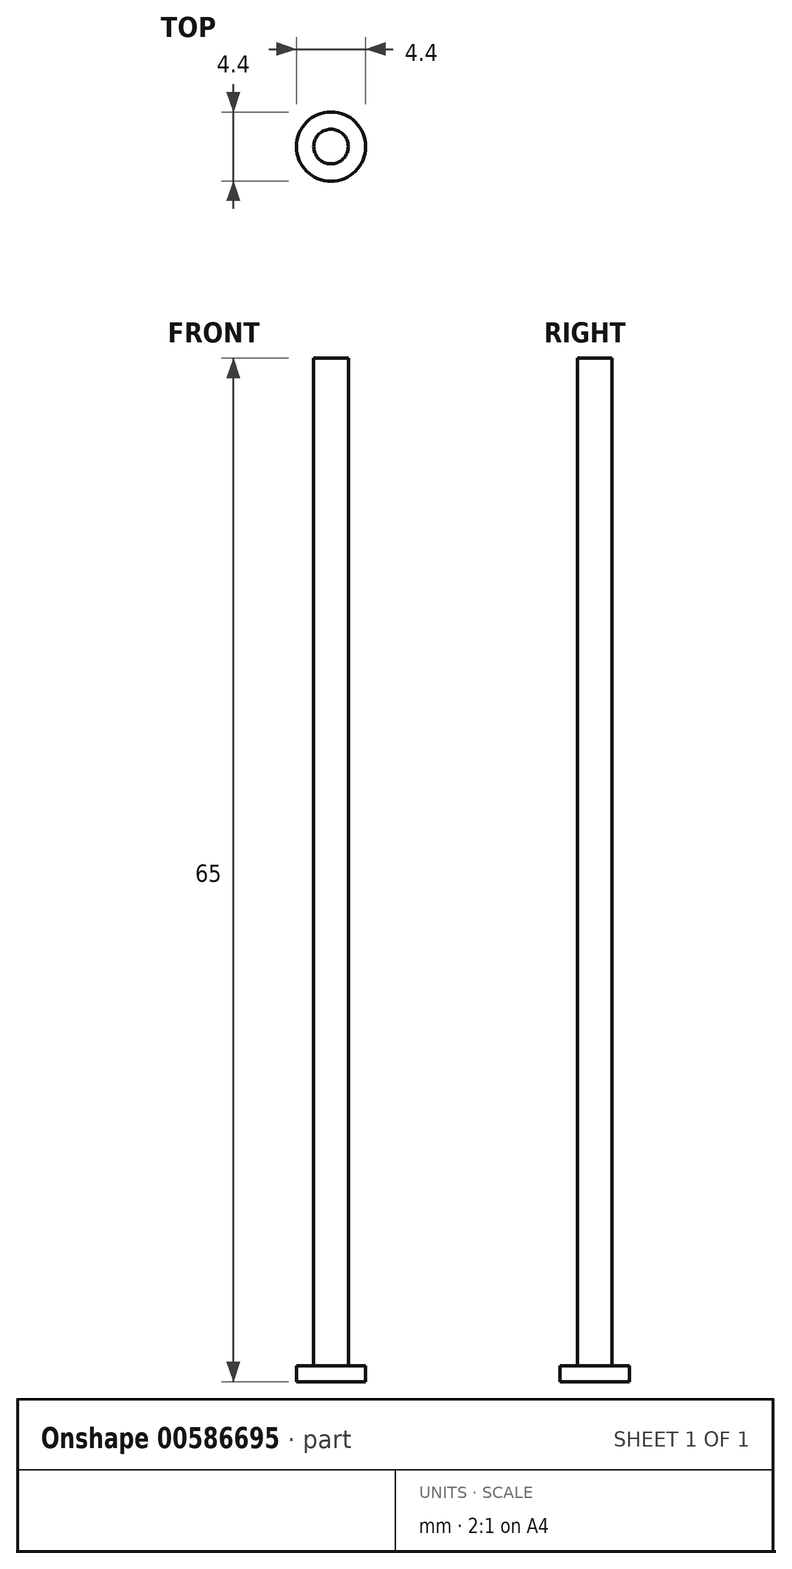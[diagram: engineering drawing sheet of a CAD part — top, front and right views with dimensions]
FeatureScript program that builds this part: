
annotation { "Feature Type Name" : "Feature", "Feature Type Description" : "" }
export const myFeature = defineFeature(function(context is Context, id is Id, definition is map)
    precondition{}
    {
        {
            var Q0;
            Q0=qCreatedBy(makeId("Top.planeOp"),FACE);
            var sketch = newSketch(context, id + "F0", { "sketchPlane" : qUnion([Q0])});
            skCircle(sketch, "E0", {"center": v(0, 0) * mm, "radius": 1.1 * mm});
            skSolve(sketch);
        }
        {
            var Q0;
            Q0 = qSketchRegion(id + "F0", true);
            extrude(context, id + "F1", {"entities" : qUnion([Q0]), "depth" : 64 * mm, "offsetDistance" : 25 * mm});
        }
        {
            var Q0;
            Q0=qCreatedBy(makeId("Top.planeOp"),FACE);
            var sketch = newSketch(context, id + "F2", { "sketchPlane" : qUnion([Q0])});
            skCircle(sketch, "E1", {"center": v(0, 0) * mm, "radius": 2.2 * mm});
            skSolve(sketch);
        }
        {
            var Q0;
            Q0=makeQuery(id+"F2.imprint","IMPRINT",FACE,{"disambiguationData":[TD([[makeQuery(id+"F2.imprint","IMPRINT",EDGE,{"derivedFrom":sQuery(id+"F2.wireOp",EDGE,"E1")}),1.0]])]});
            extrude(context, id + "F3", {"entities" : qUnion([Q0]), "operationType" : NewBodyOperationType.ADD, "oppositeDirection" : true, "depth" : 1 * mm, "offsetDistance" : 25 * mm});
        }
    });
